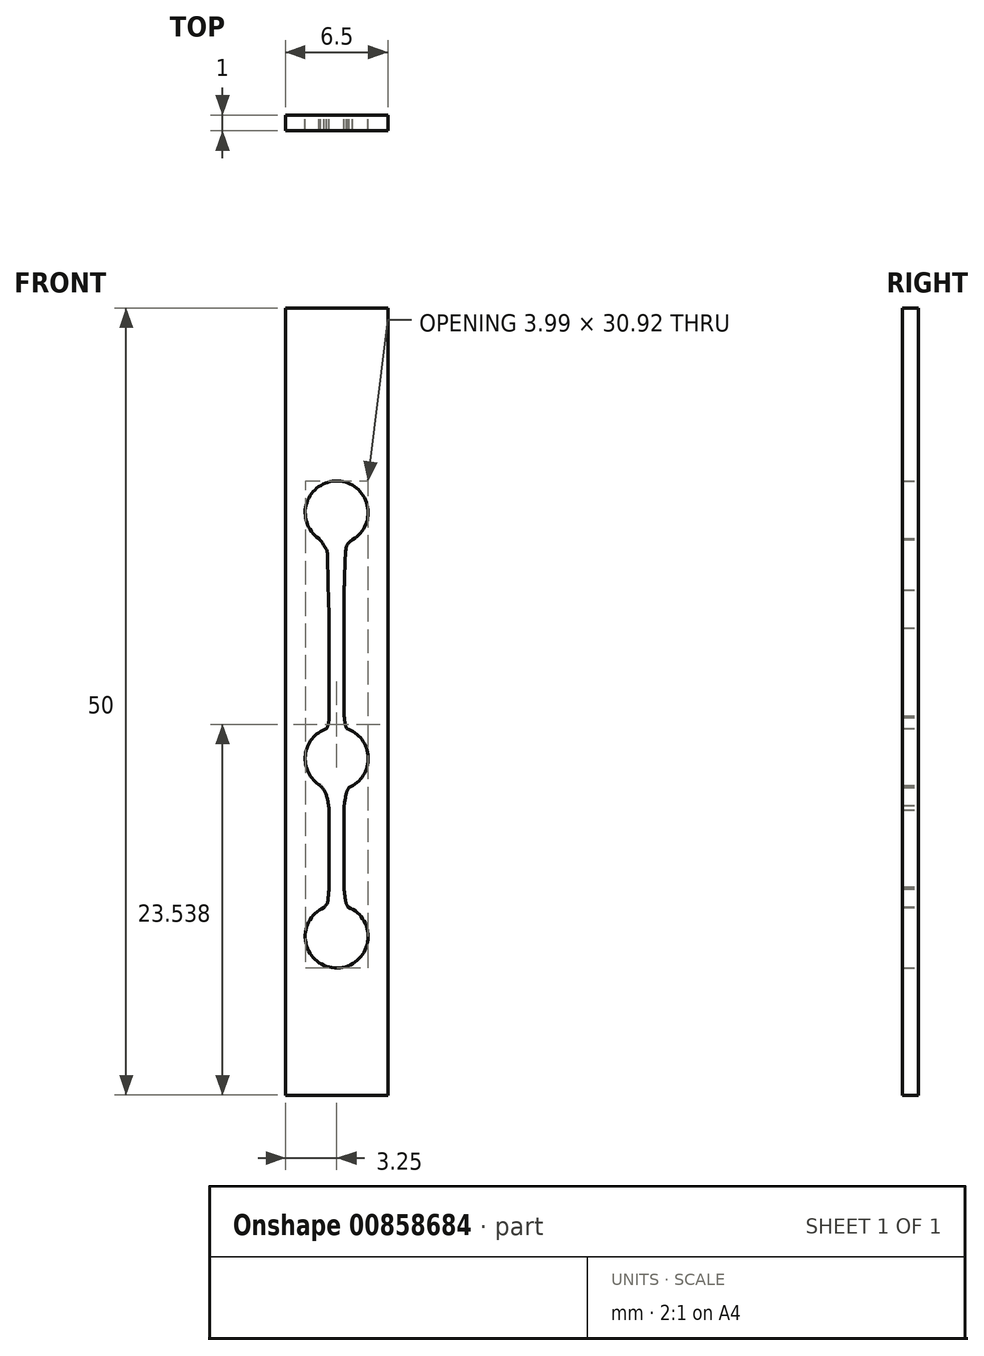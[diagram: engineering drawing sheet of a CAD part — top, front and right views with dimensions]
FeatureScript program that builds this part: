
annotation { "Feature Type Name" : "Feature", "Feature Type Description" : "" }
export const myFeature = defineFeature(function(context is Context, id is Id, definition is map)
    precondition{}
    {
        {
            var Q0;
            Q0=qCreatedBy(makeId("Front.planeOp"),FACE);
            var sketch = newSketch(context, id + "F0", { "sketchPlane" : qUnion([Q0])});
            skLineSegment(sketch, "E0.bottom", {"start": v(0.47, 38.85) * mm, "end": v(6.97, 38.85) * mm});
            skLineSegment(sketch, "E0.top", {"start": v(0.47, -11.15) * mm, "end": v(6.97, -11.15) * mm});
            skLineSegment(sketch, "E0.left", {"start": v(0.47, 38.85) * mm, "end": v(0.47, -11.15) * mm});
            skLineSegment(sketch, "E0.right", {"start": v(6.97, 38.85) * mm, "end": v(6.97, -11.15) * mm});
            skLineSegment(sketch, "E1", {"start": v(3.72, 38.85) * mm, "end": v(3.72, -11.15) * mm});
            skCircle(sketch, "E2", {"center": v(3.72, 25.85) * mm, "radius": 2 * mm});
            skCircle(sketch, "E3", {"center": v(3.72, 10.23) * mm, "radius": 2 * mm});
            skCircle(sketch, "E4", {"center": v(3.72, -1.07) * mm, "radius": 2 * mm});
            skLineSegment(sketch, "E5", {"start": v(3.24, 23.9) * mm, "end": v(3.24, 12.17) * mm});
            skLineSegment(sketch, "E6", {"start": v(4.19, 23.9) * mm, "end": v(4.19, 12.17) * mm});
            skLineSegment(sketch, "E7", {"start": v(3.24, 8.29) * mm, "end": v(3.24, 0.87) * mm});
            skLineSegment(sketch, "E8", {"start": v(4.19, 8.29) * mm, "end": v(4.19, 0.87) * mm});
            skFitSpline(sketch, "E9", {"points": [v(2.58, 24.2) * mm, v(2.9, 23.79) * mm, v(3.07, 23.46) * mm, v(3.13, 23.1) * mm, v(3.24, 18.5) * mm, v(3.24, 19.1) * mm], "startDerivative": vector(2.2, -2.78) * mm, "endDerivative": vector(-0.05, 6.36) * mm});
            skFitSpline(sketch, "E10", {"points": [v(4.73, 24.13) * mm, v(4.46, 23.9) * mm, v(4.36, 23.76) * mm, v(4.3, 23.5) * mm, v(4.19, 20.94) * mm, v(4.19, 20.95) * mm], "startDerivative": vector(-1.67, -1.21) * mm, "endDerivative": vector(0, 0.67) * mm});
            skFitSpline(sketch, "E11", {"points": [v(3.07, 12.12) * mm, v(3.16, 12.34) * mm, v(3.24, 12.82) * mm, v(3.24, 12.83) * mm], "startDerivative": vector(0.25, 0.43) * mm, "endDerivative": vector(0, 0.06) * mm});
            skFitSpline(sketch, "E12", {"points": [v(4.34, 12.13) * mm, v(4.27, 12.36) * mm, v(4.19, 12.93) * mm], "startDerivative": vector(-0.18, 0.52) * mm, "endDerivative": vector(-0.14, 1.05) * mm});
            skFitSpline(sketch, "E13", {"points": [v(4.49, 8.39) * mm, v(4.32, 7.99) * mm, v(4.19, 7.24) * mm, v(4.19, 7.3) * mm], "startDerivative": vector(-0.44, -0.78) * mm, "endDerivative": vector(0.03, 0.63) * mm});
            skFitSpline(sketch, "E14", {"points": [v(2.69, 8.51) * mm, v(3, 8.05) * mm, v(3.16, 7.47) * mm, v(3.24, 6.97) * mm], "startDerivative": vector(1.02, -1.3) * mm, "endDerivative": vector(0.22, -1.52) * mm});
            skFitSpline(sketch, "E15", {"points": [v(2.92, 0.76) * mm, v(3.11, 1.02) * mm, v(3.18, 1.4) * mm, v(3.24, 2.06) * mm, v(3.24, 2.08) * mm], "startDerivative": vector(0.83, 0.97) * mm, "endDerivative": vector(-0.02, 0.15) * mm});
            skFitSpline(sketch, "E16", {"points": [v(4.44, 0.79) * mm, v(4.32, 1.03) * mm, v(4.19, 1.93) * mm], "startDerivative": vector(-0.37, 0.55) * mm, "endDerivative": vector(-0.16, 1.62) * mm});
            skSolve(sketch);
        }
        {
            var Q0;
            {var subQ13=sQuery(id+"F0.wireOp",EDGE,"E0.right");Q0=makeQuery(id+"F0.imprint","IMPRINT",FACE,{"disambiguationData":[TD([[makeQuery(id+"F0.imprint","IMPRINT",EDGE,{"derivedFrom":subQ13}),-1.0]])]});}
            var Q1;
            {var subQ7=sQuery(id+"F0.wireOp",EDGE,"E0.left");Q1=makeQuery(id+"F0.imprint","IMPRINT",FACE,{"disambiguationData":[TD([[makeQuery(id+"F0.imprint","IMPRINT",EDGE,{"derivedFrom":subQ7}),1.0]])]});}
            extrude(context, id + "F1", {"entities" : qUnion([Q0, Q1]), "depth" : 1 * mm, "offsetDistance" : 25 * mm});
        }
    });
